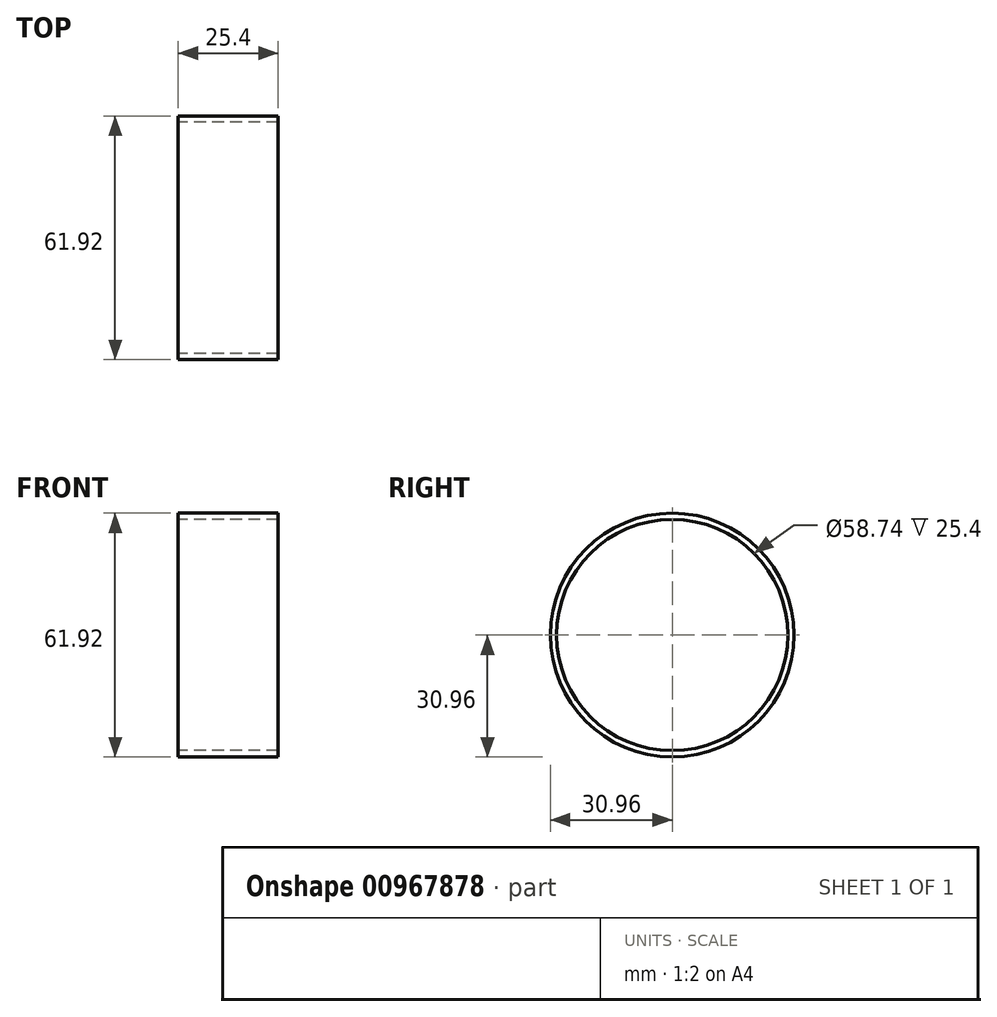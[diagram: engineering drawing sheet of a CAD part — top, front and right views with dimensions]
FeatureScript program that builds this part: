
annotation { "Feature Type Name" : "Feature", "Feature Type Description" : "" }
export const myFeature = defineFeature(function(context is Context, id is Id, definition is map)
    precondition{}
    {
        {
            var Q0;
            Q0=qCreatedBy(makeId("Right.planeOp"),FACE);
            var sketch = newSketch(context, id + "F0", { "sketchPlane" : qUnion([Q0])});
            skCircle(sketch, "E0", {"center": v(0, 0) * mm, "radius": 30.96 * mm});
            skCircle(sketch, "E1", {"center": v(0, 0) * mm, "radius": 29.37 * mm});
            skPoint(sketch, "E2", {"position": v(0, 29.37) * mm});
            skPoint(sketch, "E3", {"position": v(0, 30.96) * mm});
            skSolve(sketch);
        }
        {
            var Q0;
            Q0=makeQuery(id+"F0.imprint","IMPRINT",FACE,{"disambiguationData":[TD([[makeQuery(id+"F0.imprint","IMPRINT",EDGE,{"derivedFrom":sQuery(id+"F0.wireOp",EDGE,"E0")}),1.0]])]});
            extrude(context, id + "F1", {"entities" : qUnion([Q0]), "endBound" : BoundingType.SYMMETRIC, "depth" : 25.4 * mm, "offsetDistance" : 25.4 * mm});
        }
    });
